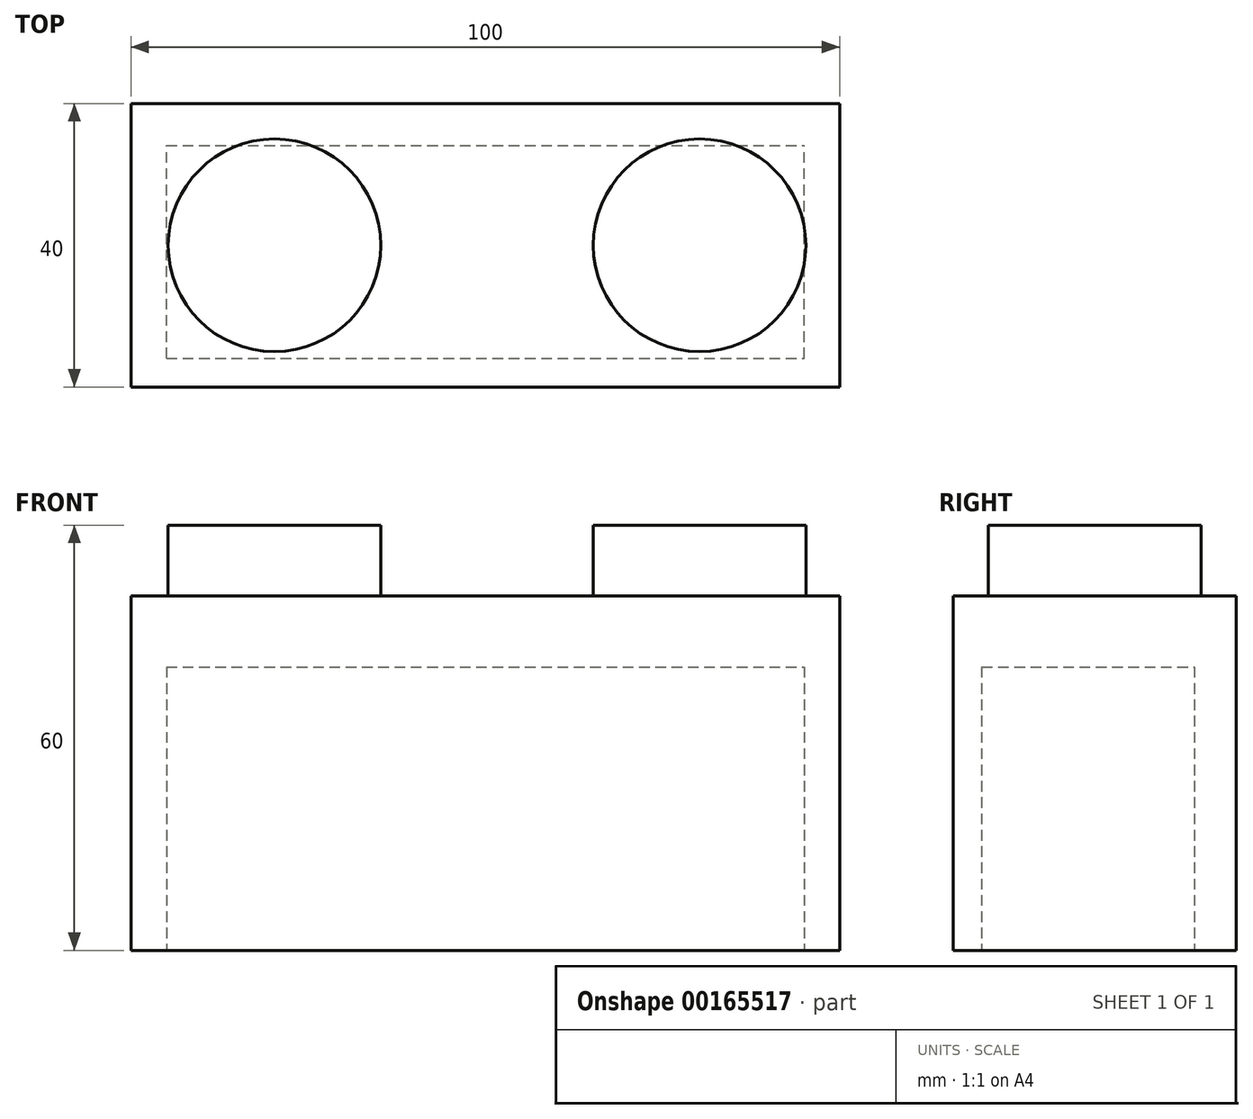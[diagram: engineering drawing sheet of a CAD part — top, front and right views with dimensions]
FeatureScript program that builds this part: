
annotation { "Feature Type Name" : "Feature", "Feature Type Description" : "" }
export const myFeature = defineFeature(function(context is Context, id is Id, definition is map)
    precondition{}
    {
        {
            var Q0;
            Q0=qCreatedBy(makeId("Front.planeOp"),FACE);
            var sketch = newSketch(context, id + "F0", { "sketchPlane" : qUnion([Q0])});
            skLineSegment(sketch, "E0.bottom", {"start": v(50, -25) * mm, "end": v(-50, -25) * mm});
            skLineSegment(sketch, "E0.top", {"start": v(50, 25) * mm, "end": v(-50, 25) * mm});
            skLineSegment(sketch, "E0.left", {"start": v(50, -25) * mm, "end": v(50, 25) * mm});
            skLineSegment(sketch, "E0.right", {"start": v(-50, -25) * mm, "end": v(-50, 25) * mm});
            skPoint(sketch, "E0.middle", {"position": v(0, 0) * mm});
            skSolve(sketch);
        }
        {
            var Q0;
            Q0=makeQuery(id+"F0.imprint","IMPRINT",FACE,{"disambiguationData":[TD([[makeQuery(id+"F0.imprint","IMPRINT",EDGE,{"derivedFrom":sQuery(id+"F0.wireOp",EDGE,"E0.bottom")}),-1.0]])]});
            extrude(context, id + "F1", {"entities" : qUnion([Q0]), "depth" : 40 * mm});
        }
        {
            var Q0;
            Q0=makeQuery(id+"F1.opExtrude","SWEPT_FACE",FACE,{"disambiguationData":[OSD([sQuery(id+"F0.wireOp",EDGE,"E0.top")])]});
            var sketch = newSketch(context, id + "F2", { "sketchPlane" : qUnion([Q0])});
            skCircle(sketch, "E1", {"center": v(-29.76, -20) * mm, "radius": 15 * mm});
            skPoint(sketch, "E1.centerSnap0", {"position": v(-50, -20) * mm});
            skCircle(sketch, "E2", {"center": v(30.24, -20) * mm, "radius": 15 * mm});
            skPoint(sketch, "E2.centerSnap0", {"position": v(50, -20) * mm});
            skSolve(sketch);
        }
        {
            var Q0;
            Q0 = qSketchRegion(id + "F2", true);
            extrude(context, id + "F3", {"entities" : qUnion([Q0]), "operationType" : NewBodyOperationType.ADD, "depth" : 10 * mm});
        }
        {
            var Q0;
            Q0=makeQuery(id+"F1.opExtrude","SWEPT_FACE",FACE,{"disambiguationData":[OSD([sQuery(id+"F0.wireOp",EDGE,"E0.bottom")])]});
            var sketch = newSketch(context, id + "F4", { "sketchPlane" : qUnion([Q0])});
            skLineSegment(sketch, "E3.bottom", {"start": v(-50, 40) * mm, "end": v(50, 40) * mm});
            skLineSegment(sketch, "E3.top", {"start": v(-50, 0) * mm, "end": v(50, 0) * mm});
            skLineSegment(sketch, "E3.left", {"start": v(-50, 40) * mm, "end": v(-50, 0) * mm});
            skLineSegment(sketch, "E3.right", {"start": v(50, 40) * mm, "end": v(50, 0) * mm});
            skSolve(sketch);
        }
        {
            var Q0;
            Q0=makeQuery(id+"F4.imprint","IMPRINT",FACE,{"disambiguationData":[TD([[makeQuery(id+"F4.imprint","IMPRINT",EDGE,{"derivedFrom":sQuery(id+"F4.wireOp",EDGE,"E3.bottom")}),1.0]])]});
            var sketch = newSketch(context, id + "F5", { "sketchPlane" : qUnion([Q0])});
            skLineSegment(sketch, "E4.bottom", {"start": v(-45, 35.95) * mm, "end": v(45, 35.95) * mm});
            skLineSegment(sketch, "E4.top", {"start": v(-45, 5.95) * mm, "end": v(45, 5.95) * mm});
            skLineSegment(sketch, "E4.left", {"start": v(-45, 35.95) * mm, "end": v(-45, 5.95) * mm});
            skLineSegment(sketch, "E4.right", {"start": v(45, 35.95) * mm, "end": v(45, 5.95) * mm});
            skSolve(sketch);
        }
        {
            var Q0;
            Q0 = qSketchRegion(id + "F5", true);
            extrude(context, id + "F6", {"entities" : qUnion([Q0]), "operationType" : NewBodyOperationType.REMOVE, "oppositeDirection" : true, "depth" : 40 * mm});
        }
    });
